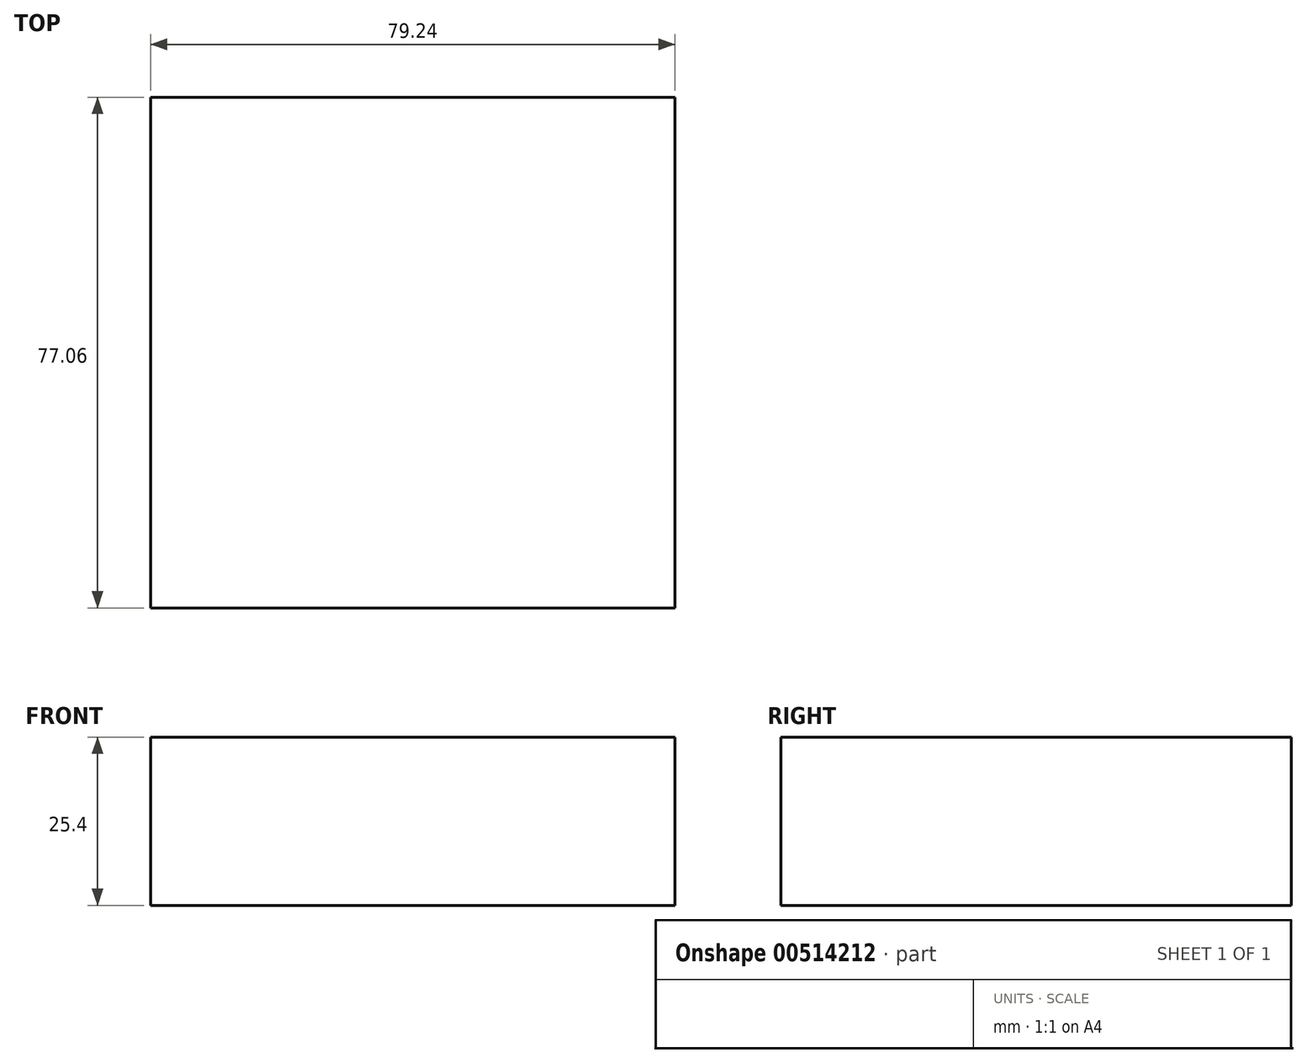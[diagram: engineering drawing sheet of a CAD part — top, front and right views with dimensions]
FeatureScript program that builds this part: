
annotation { "Feature Type Name" : "Feature", "Feature Type Description" : "" }
export const myFeature = defineFeature(function(context is Context, id is Id, definition is map)
    precondition{}
    {
        {
            var Q0;
            Q0=qCreatedBy(makeId("Top.planeOp"),FACE);
            var sketch = newSketch(context, id + "F0", { "sketchPlane" : qUnion([Q0])});
            skLineSegment(sketch, "E0.bottom", {"start": v(-39.62, 38.53) * mm, "end": v(39.62, 38.53) * mm});
            skLineSegment(sketch, "E0.top", {"start": v(-39.62, -38.53) * mm, "end": v(39.62, -38.53) * mm});
            skLineSegment(sketch, "E0.left", {"start": v(-39.62, 38.53) * mm, "end": v(-39.62, -38.53) * mm});
            skLineSegment(sketch, "E0.right", {"start": v(39.62, 38.53) * mm, "end": v(39.62, -38.53) * mm});
            skPoint(sketch, "E0.middle", {"position": v(0, 0) * mm});
            skSolve(sketch);
        }
        {
            var Q0;
            Q0=makeQuery(id+"F0.imprint","IMPRINT",FACE,{"disambiguationData":[TD([[makeQuery(id+"F0.imprint","IMPRINT",EDGE,{"derivedFrom":sQuery(id+"F0.wireOp",EDGE,"E0.bottom")}),-1.0]])]});
            extrude(context, id + "F1", {"entities" : qUnion([Q0]), "depth" : 25.4 * mm});
        }
    });
